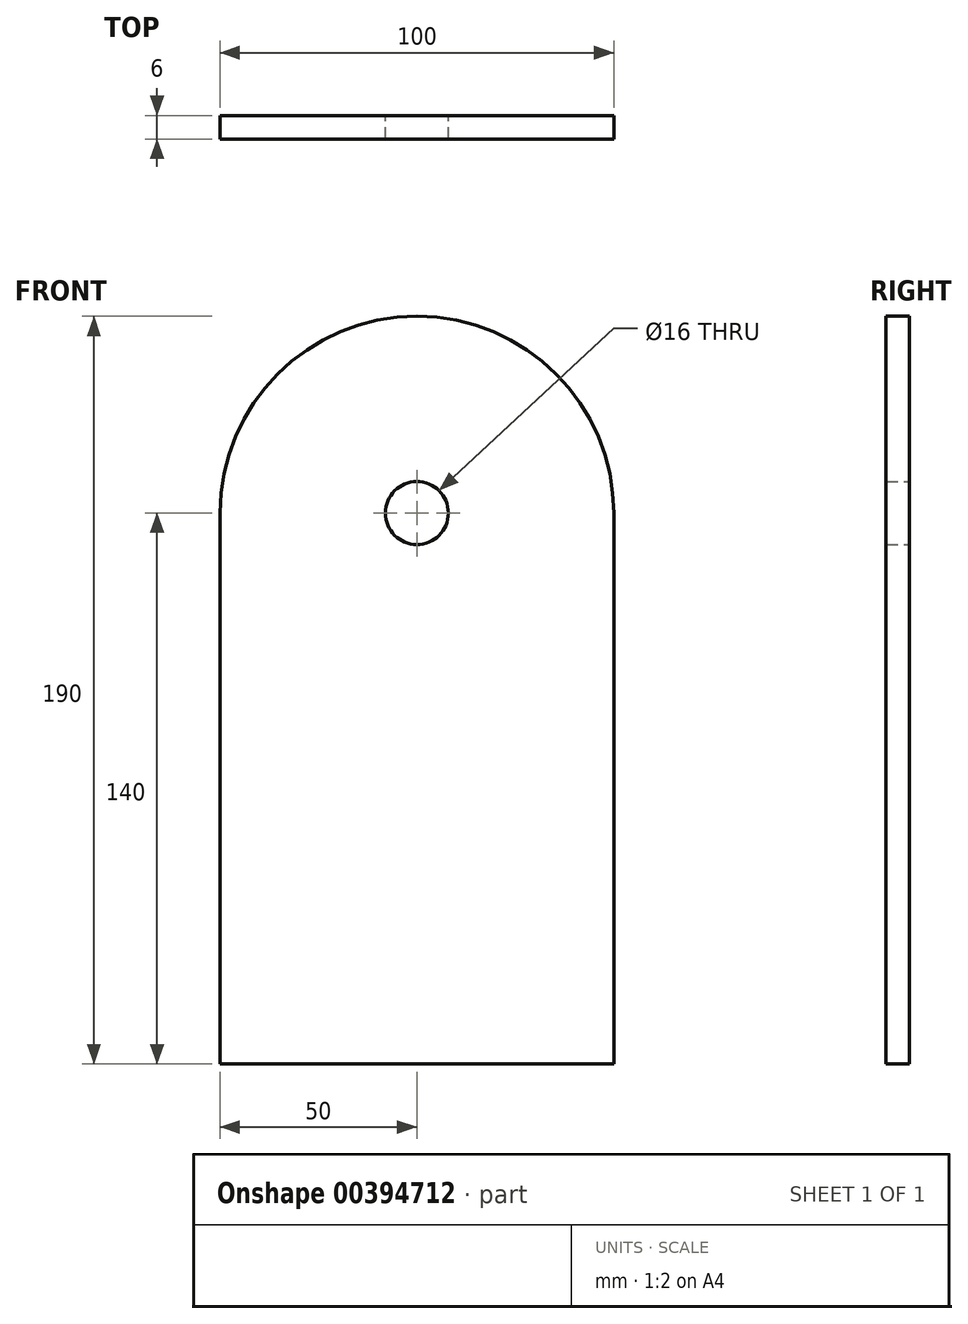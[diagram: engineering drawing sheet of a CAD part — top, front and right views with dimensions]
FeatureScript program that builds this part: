
annotation { "Feature Type Name" : "Feature", "Feature Type Description" : "" }
export const myFeature = defineFeature(function(context is Context, id is Id, definition is map)
    precondition{}
    {
        {
            var Q0;
            Q0=qCreatedBy(makeId("Front.planeOp"),FACE);
            var sketch = newSketch(context, id + "F0", { "sketchPlane" : qUnion([Q0])});
            skCircle(sketch, "E0", {"center": v(0, 0) * mm, "radius": 8 * mm});
            skLineSegment(sketch, "E1", {"start": v(-50, 0) * mm, "end": v(-50, -140) * mm});
            skLineSegment(sketch, "E2", {"start": v(-50, -140) * mm, "end": v(50, -140) * mm});
            skLineSegment(sketch, "E3", {"start": v(50, 0) * mm, "end": v(50, -140) * mm});
            skArc(sketch, "E4", {"start": v(-50, 0) * mm, "mid": v(0, 50) * mm, "end": v(50, 0) * mm});
            skSolve(sketch);
        }
        {
            var Q0;
            Q0=makeQuery(id+"F0.imprint","IMPRINT",FACE,{"disambiguationData":[TD([[makeQuery(id+"F0.imprint","IMPRINT",EDGE,{"derivedFrom":sQuery(id+"F0.wireOp",EDGE,"E0")}),-1.0]])]});
            extrude(context, id + "F1", {"entities" : qUnion([Q0]), "depth" : 6 * mm});
        }
    });
